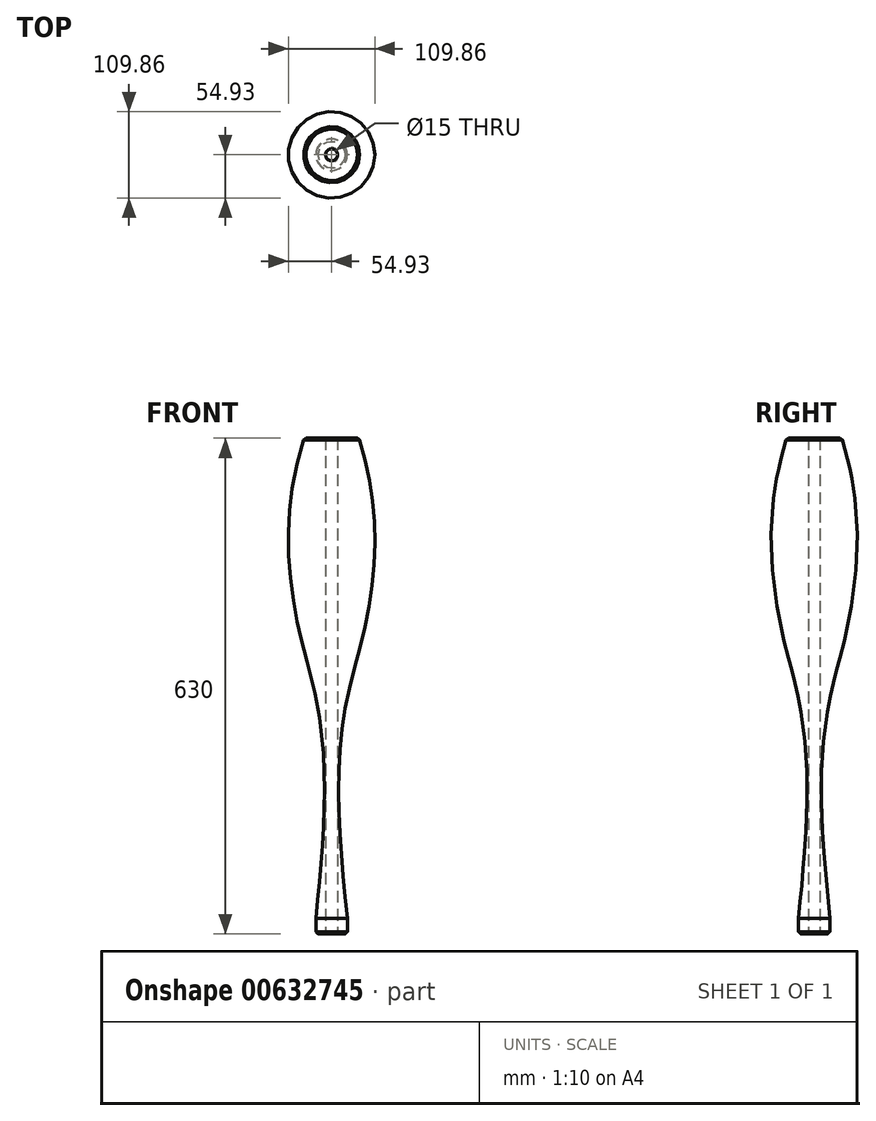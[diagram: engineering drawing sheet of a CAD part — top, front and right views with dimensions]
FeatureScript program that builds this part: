
annotation { "Feature Type Name" : "Feature", "Feature Type Description" : "" }
export const myFeature = defineFeature(function(context is Context, id is Id, definition is map)
    precondition{}
    {
        {
            var Q0;
            Q0=qCreatedBy(makeId("Top.planeOp"),FACE);
            cPlane(context, id + "F0", {"entities" : qUnion([Q0]), "cplaneType" : CPlaneType.OFFSET, "offset" : 280 * mm, "width" : 150 * mm, "height" : 150 * mm});
        }
        {
            var Q0;
            Q0=qCreatedBy(id+"F0.planeOp",FACE);
            cPlane(context, id + "F1", {"entities" : qUnion([Q0]), "cplaneType" : CPlaneType.OFFSET, "offset" : 80 * mm, "width" : 150 * mm, "height" : 150 * mm});
        }
        {
            var Q0;
            Q0=qCreatedBy(id+"F1.planeOp",FACE);
            cPlane(context, id + "F2", {"entities" : qUnion([Q0]), "cplaneType" : CPlaneType.OFFSET, "offset" : 200 * mm, "width" : 150 * mm, "height" : 150 * mm});
        }
        {
            var Q0;
            Q0=qCreatedBy(id+"F2.planeOp",FACE);
            cPlane(context, id + "F3", {"entities" : qUnion([Q0]), "cplaneType" : CPlaneType.OFFSET, "offset" : 50 * mm, "width" : 150 * mm, "height" : 150 * mm});
        }
        {
            var Q0;
            Q0=qCreatedBy(makeId("Top.planeOp"),FACE);
            var sketch = newSketch(context, id + "F4", { "sketchPlane" : qUnion([Q0])});
            skCircle(sketch, "E0", {"center": v(0, 0) * mm, "radius": 20 * mm});
            skSolve(sketch);
        }
        {
            var Q0;
            Q0=qCreatedBy(id+"F0.planeOp",FACE);
            var sketch = newSketch(context, id + "F5", { "sketchPlane" : qUnion([Q0])});
            skCircle(sketch, "E1", {"center": v(0, 0) * mm, "radius": 20 * mm});
            skSolve(sketch);
        }
        {
            var Q0;
            Q0=qCreatedBy(id+"F1.planeOp",FACE);
            var sketch = newSketch(context, id + "F6", { "sketchPlane" : qUnion([Q0])});
            skCircle(sketch, "E2", {"center": v(0, 0) * mm, "radius": 40 * mm});
            skSolve(sketch);
        }
        {
            var Q0;
            Q0=qCreatedBy(id+"F2.planeOp",FACE);
            var sketch = newSketch(context, id + "F7", { "sketchPlane" : qUnion([Q0])});
            skCircle(sketch, "E3", {"center": v(0, 0) * mm, "radius": 47.5 * mm});
            skSolve(sketch);
        }
        {
            var Q0;
            Q0=qCreatedBy(id+"F3.planeOp",FACE);
            var sketch = newSketch(context, id + "F8", { "sketchPlane" : qUnion([Q0])});
            skCircle(sketch, "E4", {"center": v(0, 0) * mm, "radius": 35 * mm});
            skSolve(sketch);
        }
        {
            var Q0;
            Q0=makeQuery(id+"F8.imprint","IMPRINT",FACE,{"disambiguationData":[TD([[makeQuery(id+"F8.imprint","IMPRINT",EDGE,{"derivedFrom":sQuery(id+"F8.wireOp",EDGE,"E4")}),1.0]])]});
            var Q1;
            Q1=makeQuery(id+"F7.imprint","IMPRINT",FACE,{"disambiguationData":[TD([[makeQuery(id+"F7.imprint","IMPRINT",EDGE,{"derivedFrom":sQuery(id+"F7.wireOp",EDGE,"E3")}),1.0]])]});
            var Q2;
            Q2=makeQuery(id+"F6.imprint","IMPRINT",FACE,{"disambiguationData":[TD([[makeQuery(id+"F6.imprint","IMPRINT",EDGE,{"derivedFrom":sQuery(id+"F6.wireOp",EDGE,"E2")}),1.0]])]});
            var Q3;
            Q3=makeQuery(id+"F5.imprint","IMPRINT",FACE,{"disambiguationData":[TD([[makeQuery(id+"F5.imprint","IMPRINT",EDGE,{"derivedFrom":sQuery(id+"F5.wireOp",EDGE,"E1")}),1.0]])]});
            var Q4;
            Q4=makeQuery(id+"F4.imprint","IMPRINT",FACE,{"disambiguationData":[TD([[makeQuery(id+"F4.imprint","IMPRINT",EDGE,{"derivedFrom":sQuery(id+"F4.wireOp",EDGE,"E0")}),1.0]])]});
            loft(context, id + "F9", {"sheetProfilesArray" : [{ "sheetProfileEntities" : qUnion([Q0]) }, { "sheetProfileEntities" : qUnion([Q1]) }, { "sheetProfileEntities" : qUnion([Q2]) }, { "sheetProfileEntities" : qUnion([Q3]) }, { "sheetProfileEntities" : qUnion([Q4]) }]});
        }
        {
            var Q0;
            Q0=makeQuery(id+"F9.opLoft","CAP_FACE",FACE,{"disambiguationData":[OSD([makeQuery(id+"F4.imprint","IMPRINT",FACE,{"disambiguationData":[TD([[makeQuery(id+"F4.imprint","IMPRINT",EDGE,{"derivedFrom":sQuery(id+"F4.wireOp",EDGE,"E0")}),1.0]])]})])],"isStart":true});
            extrude(context, id + "F10", {"entities" : qUnion([Q0]), "operationType" : NewBodyOperationType.ADD, "depth" : 20 * mm, "offsetDistance" : 25 * mm});
        }
        {
            var Q0;
            Q0=makeQuery(id+"F10.opExtrude","CAP_EDGE",EDGE,{"disambiguationData":[OSD([sQuery(id+"F4.wireOp",EDGE,"E0"),sQuery(id+"F8.wireOp",EDGE,"E4")])],"isStart":false});
            var Q1;
            Q1=makeQuery(id+"F9.opLoft","MID_CAP_EDGE",EDGE,{"disambiguationData":[OSD([sQuery(id+"F8.wireOp",EDGE,"E4")])],"capPos":0.0});
            chamfer(context, id + "F11", {"entities" : qUnion([Q0, Q1]), "width" : 3 * mm, "tangentPropagation" : true});
        }
        {
            var Q0;
            Q0=makeQuery(id+"F10.opExtrude","CAP_FACE",FACE,{"disambiguationData":[OSD([makeQuery(id+"F4.imprint","IMPRINT",FACE,{"disambiguationData":[TD([[makeQuery(id+"F4.imprint","IMPRINT",EDGE,{"derivedFrom":sQuery(id+"F4.wireOp",EDGE,"E0")}),1.0]])]})])],"isStart":false});
            var sketch = newSketch(context, id + "F12", { "sketchPlane" : qUnion([Q0])});
            skPoint(sketch, "E5", {"position": v(0, 0) * mm});
            skSolve(sketch);
        }
        {
            var Q0;
            Q0=sQuery(id+"F12.wireOp",VERTEX,"E5");
            var Q1;
            Q1=makeQuery(id+"F9.opLoft","SWEPT_BODY",BODY,{"disambiguationData":[OSD([makeQuery(id+"F4.imprint","IMPRINT",FACE,{"disambiguationData":[TD([[makeQuery(id+"F4.imprint","IMPRINT",EDGE,{"derivedFrom":sQuery(id+"F4.wireOp",EDGE,"E0")}),1.0]])]}),sQuery(id+"F5.wireOp",EDGE,"E1"),sQuery(id+"F6.wireOp",EDGE,"E2"),sQuery(id+"F7.wireOp",EDGE,"E3"),makeQuery(id+"F8.imprint","IMPRINT",FACE,{"disambiguationData":[TD([[makeQuery(id+"F8.imprint","IMPRINT",EDGE,{"derivedFrom":sQuery(id+"F8.wireOp",EDGE,"E4")}),1.0]])]})])]});
            hole(context, id + "F13", {"style" : HoleStyle.SIMPLE, "endStyle" : HoleEndStyle.THROUGH, "holeDiameter" : 15 * mm, "majorDiameter" : 5 * mm, "isTappedThrough" : true, "tappedDepth" : 12 * mm, "tapClearance" : 3, "startFromSketch" : true, "locations" : qUnion([Q0]), "scope" : qUnion([Q1])});
        }
    });
